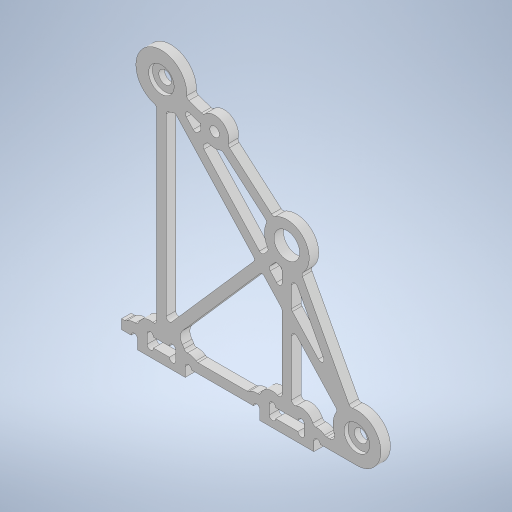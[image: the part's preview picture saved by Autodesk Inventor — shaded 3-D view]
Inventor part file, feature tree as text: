
AUTODESK INVENTOR PART (.ipt)
format: ipt  version: 2023.1 (Build 271208000, 208)  size: 506,368 bytes
history: native  units: mm
features: extrude x2, other x1, sketch x1, fillet x1
ambient origin geometry x8: Origin, YZ Plane, XZ Plane, XY Plane, X Axis, Y Axis, Z Axis, Center Point
bodies: Body1 (feature_tree)
feature tree (5):
  other  "ソリッド1"
  sketch  "スケッチ1"
  extrude  "押し出し1"  Depth=3.0mm TaperAngle=0.0deg
  extrude  "押し出し2"  Depth=4.0mm
  fillet  "フィレット1"  Radius=1.8mm
